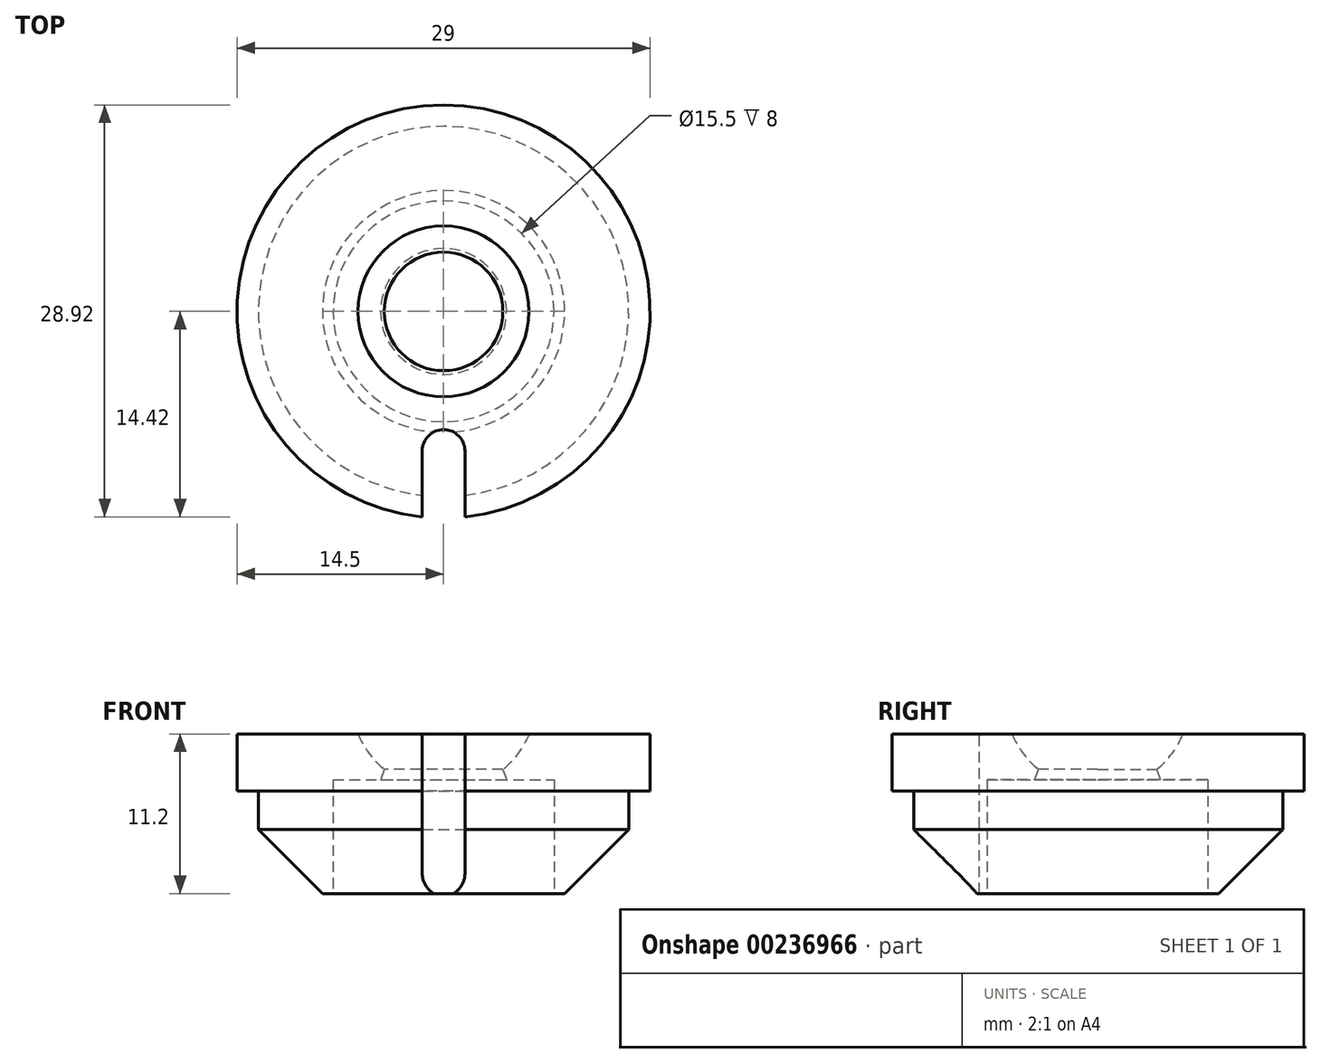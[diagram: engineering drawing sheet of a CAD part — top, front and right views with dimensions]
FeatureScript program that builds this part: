
annotation { "Feature Type Name" : "Feature", "Feature Type Description" : "" }
export const myFeature = defineFeature(function(context is Context, id is Id, definition is map)
    precondition{}
    {
        {
            var Q0;
            Q0=qCreatedBy(makeId("Top.planeOp"),FACE);
            var sketch = newSketch(context, id + "F0", { "sketchPlane" : qUnion([Q0])});
            skCircle(sketch, "E0", {"center": v(0, 0) * mm, "radius": 14.5 * mm});
            skSolve(sketch);
        }
        {
            var Q0;
            Q0 = qSketchRegion(id + "F0", true);
            extrude(context, id + "F1", {"entities" : qUnion([Q0]), "depth" : 4 * mm});
        }
        {
            var Q0;
            Q0=makeQuery(id+"F1.opExtrude","CAP_FACE",FACE,{"disambiguationData":[OSD([sQuery(id+"F0.wireOp",EDGE,"E0")])],"isStart":true});
            var sketch = newSketch(context, id + "F2", { "sketchPlane" : qUnion([Q0])});
            skCircle(sketch, "E1", {"center": v(0, 0) * mm, "radius": 13 * mm});
            skSolve(sketch);
        }
        {
            var Q0;
            Q0 = qSketchRegion(id + "F2", true);
            extrude(context, id + "F3", {"entities" : qUnion([Q0]), "operationType" : NewBodyOperationType.ADD, "depth" : 8.2 * mm});
        }
        {
            var Q0;
            Q0=makeQuery(id+"F3.opExtrude","CAP_EDGE",EDGE,{"disambiguationData":[OSD([sQuery(id+"F2.wireOp",EDGE,"E1")])],"isStart":false});
            chamfer(context, id + "F4", {"entities" : qUnion([Q0]), "width" : 5.5 * mm, "tangentPropagation" : true});
        }
        {
            var Q0;
            Q0=makeQuery(id+"F3.opExtrude","CAP_FACE",FACE,{"disambiguationData":[OSD([sQuery(id+"F2.wireOp",EDGE,"E1")])],"isStart":false});
            var sketch = newSketch(context, id + "F5", { "sketchPlane" : qUnion([Q0])});
            skCircle(sketch, "E2", {"center": v(0, 0) * mm, "radius": 7.75 * mm});
            skSolve(sketch);
        }
        {
            var Q0;
            Q0 = qSketchRegion(id + "F5", true);
            extrude(context, id + "F6", {"entities" : qUnion([Q0]), "operationType" : NewBodyOperationType.REMOVE, "oppositeDirection" : true, "depth" : 9 * mm});
        }
        {
            var Q0;
            Q0=makeQuery(id+"F6.boolean.opBoolean","COPY",FACE,{"derivedFrom":makeQuery(id+"F6.opExtrude","CAP_FACE",FACE,{"disambiguationData":[OSD([sQuery(id+"F5.wireOp",EDGE,"E2")])],"isStart":false})});
            var sketch = newSketch(context, id + "F7", { "sketchPlane" : qUnion([Q0])});
            skCircle(sketch, "E3", {"center": v(0, -0.71) * mm, "radius": 19.44 * mm});
            skSolve(sketch);
        }
        {
            var Q0;
            Q0 = qSketchRegion(id + "F7", true);
            extrude(context, id + "F8", {"entities" : qUnion([Q0]), "operationType" : NewBodyOperationType.REMOVE, "depth" : 25 * mm, "hasSecondDirection" : true, "secondDirectionOppositeDirection" : false, "secondDirectionDepth" : 8 * mm});
        }
        {
            var Q0;
            Q0=qCreatedBy(makeId("Right.planeOp"),FACE);
            var sketch = newSketch(context, id + "F9", { "sketchPlane" : qUnion([Q0])});
            skCircle(sketch, "E4", {"center": v(0, 6.5) * mm, "radius": 6.5 * mm});
            skLineSegment(sketch, "E5", {"start": v(0, 13) * mm, "end": v(0, 0) * mm});
            skSolve(sketch);
        }
        {
            var Q0;
            {var subQ0=sQuery(id+"F9.wireOp",EDGE,"E5");Q0=makeQuery(id+"F9.imprint","IMPRINT",FACE,{"disambiguationData":[TD([[makeQuery(id+"F9.imprint","IMPRINT",EDGE,{"derivedFrom":subQ0}),1.0]])]});}
            var Q1;
            Q1=sQuery(id+"F9.wireOp",EDGE,"E5");
            revolve(context, id + "F10", {"operationType" : NewBodyOperationType.REMOVE, "entities" : qUnion([Q0]), "axis" : qUnion([Q1]), "revolveType" : RevolveType.FULL, "oppositeDirection" : true});
        }
        {
            var Q0;
            Q0=makeQuery(id+"F10.boolean.opBoolean","INTERSECT",EDGE,{"derivedFrom":[makeQuery(id+"F6.boolean.opBoolean","COPY",FACE,{"derivedFrom":makeQuery(id+"F6.opExtrude","CAP_FACE",FACE,{"disambiguationData":[OSD([sQuery(id+"F5.wireOp",EDGE,"E2")])],"isStart":false})}),makeQuery(id+"F10.opRevolve","SWEPT_FACE",FACE,{"disambiguationData":[OSD([sQuery(id+"F9.wireOp",EDGE,"E4")])]})]});
            chamfer(context, id + "F11", {"entities" : qUnion([Q0]), "width" : 0.4 * mm, "tangentPropagation" : true});
        }
        {
            var Q0;
            Q0=makeQuery(id+"F1.opExtrude","CAP_FACE",FACE,{"disambiguationData":[OSD([sQuery(id+"F0.wireOp",EDGE,"E0")])],"isStart":false});
            var sketch = newSketch(context, id + "F12", { "sketchPlane" : qUnion([Q0])});
            skLineSegment(sketch, "E6.bottom", {"start": v(1.5, -8.3) * mm, "end": v(-1.5, -8.3) * mm});
            skLineSegment(sketch, "E6.top", {"start": v(1.5, -20.7) * mm, "end": v(-1.5, -20.7) * mm});
            skLineSegment(sketch, "E6.left", {"start": v(1.5, -8.3) * mm, "end": v(1.5, -20.7) * mm});
            skLineSegment(sketch, "E6.right", {"start": v(-1.5, -8.3) * mm, "end": v(-1.5, -20.7) * mm});
            skPoint(sketch, "E6.middle", {"position": v(0, -14.5) * mm});
            skSolve(sketch);
        }
        {
            var Q0;
            Q0 = qSketchRegion(id + "F12", true);
            extrude(context, id + "F13", {"entities" : qUnion([Q0]), "operationType" : NewBodyOperationType.REMOVE, "oppositeDirection" : true, "depth" : 25 * mm});
        }
        {
            var Q0;
            Q0=makeQuery(id+"F13.boolean.opBoolean","COPY",EDGE,{"derivedFrom":makeQuery(id+"F13.opExtrude","SWEPT_EDGE",EDGE,{"disambiguationData":[OSD([sQuery(id+"F12.wireOp",EDGE,"E6.bottom"),sQuery(id+"F12.wireOp",EDGE,"E6.left")])]})});
            var Q1;
            Q1=makeQuery(id+"F13.boolean.opBoolean","COPY",EDGE,{"derivedFrom":makeQuery(id+"F13.opExtrude","SWEPT_EDGE",EDGE,{"disambiguationData":[OSD([sQuery(id+"F12.wireOp",EDGE,"E6.bottom"),sQuery(id+"F12.wireOp",EDGE,"E6.right")])]})});
            fillet(context, id + "F14", {"entities" : qUnion([Q0, Q1]), "radius" : 1.5 * mm, "tangentPropagation" : true, "allowEdgeOverflow" : false});
        }
    });
